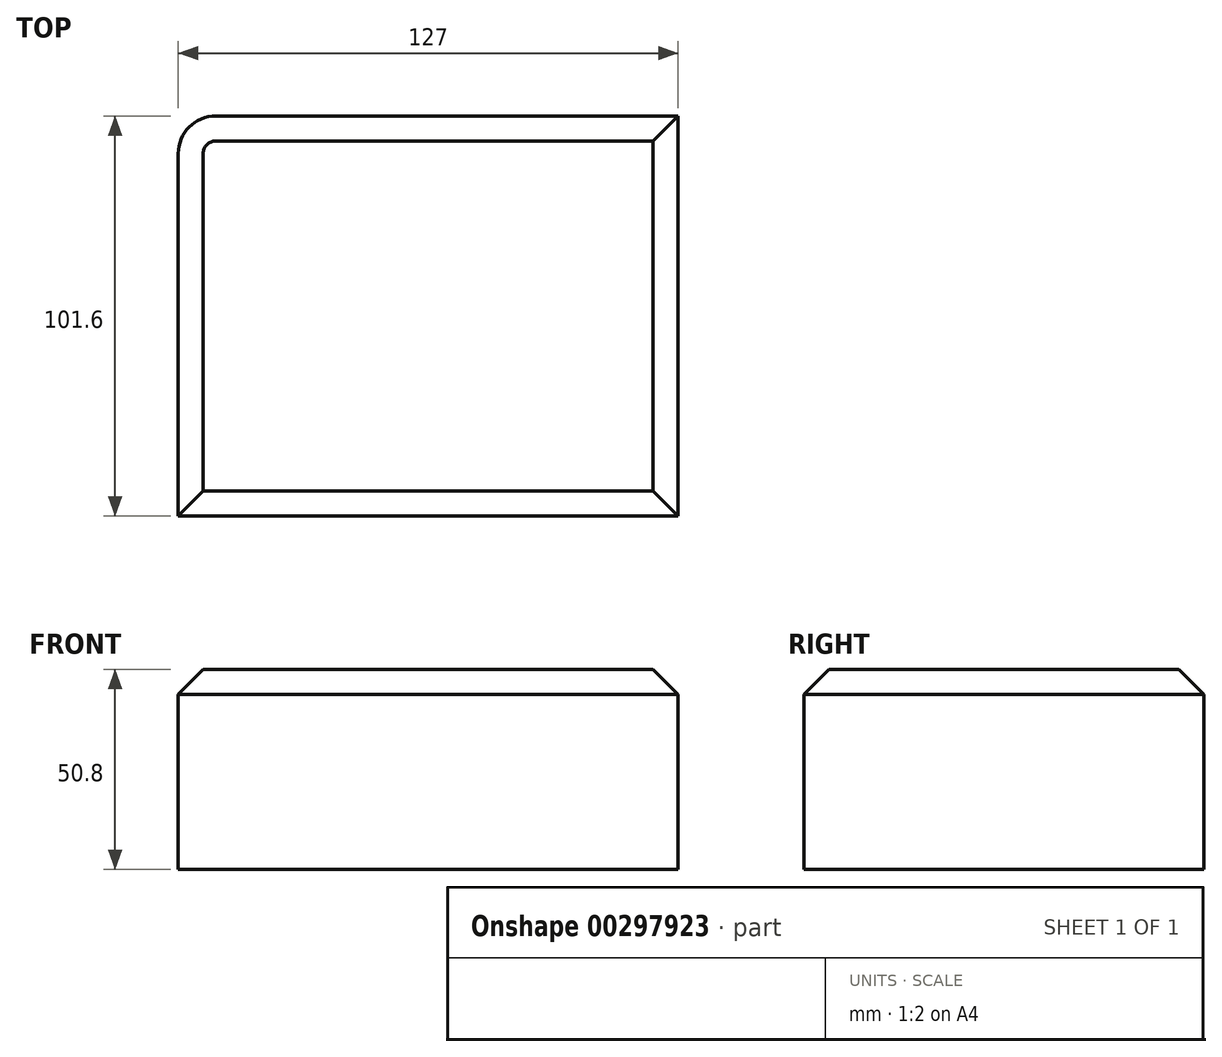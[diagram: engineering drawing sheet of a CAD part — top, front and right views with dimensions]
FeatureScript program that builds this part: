
annotation { "Feature Type Name" : "Feature", "Feature Type Description" : "" }
export const myFeature = defineFeature(function(context is Context, id is Id, definition is map)
    precondition{}
    {
        {
            var Q0;
            Q0=qCreatedBy(makeId("Top.planeOp"),FACE);
            var sketch = newSketch(context, id + "F0", { "sketchPlane" : qUnion([Q0])});
            skLineSegment(sketch, "E0.bottom", {"start": v(-53.97, 49.1) * mm, "end": v(63.5, 49.1) * mm});
            skLineSegment(sketch, "E0.top", {"start": v(-63.5, -52.5) * mm, "end": v(63.5, -52.5) * mm});
            skLineSegment(sketch, "E0.left", {"start": v(-63.5, 39.57) * mm, "end": v(-63.5, -52.5) * mm});
            skLineSegment(sketch, "E0.right", {"start": v(63.5, 49.1) * mm, "end": v(63.5, -52.5) * mm});
            skPoint(sketch, "E0.middle", {"position": v(0, -1.7) * mm});
            skPoint(sketch, "E1.visualSharp", {"position": v(-63.5, 49.1) * mm});
            skArc(sketch, "E1.filletArc", {"start": v(-53.97, 49.1) * mm, "mid": v(-60.71, 46.3) * mm, "end": v(-63.5, 39.57) * mm});
            skSolve(sketch);
        }
        {
            var Q0;
            Q0=makeQuery(id+"F0.imprint","IMPRINT",FACE,{"disambiguationData":[TD([[makeQuery(id+"F0.imprint","IMPRINT",EDGE,{"derivedFrom":sQuery(id+"F0.wireOp",EDGE,"E0.bottom")}),-1.0]])]});
            extrude(context, id + "F1", {"entities" : qUnion([Q0]), "depth" : 50.8 * mm});
        }
        {
            var Q0;
            Q0=makeQuery(id+"F1.opExtrude","CAP_EDGE",EDGE,{"disambiguationData":[OSD([sQuery(id+"F0.wireOp",EDGE,"E0.top")])],"isStart":false});
            var Q1;
            Q1=makeQuery(id+"F1.opExtrude","CAP_EDGE",EDGE,{"disambiguationData":[OSD([sQuery(id+"F0.wireOp",EDGE,"E0.right")])],"isStart":false});
            var Q2;
            Q2=makeQuery(id+"F1.opExtrude","CAP_EDGE",EDGE,{"disambiguationData":[OSD([sQuery(id+"F0.wireOp",EDGE,"E0.bottom")])],"isStart":false});
            var Q3;
            Q3=makeQuery(id+"F1.opExtrude","CAP_EDGE",EDGE,{"disambiguationData":[OSD([sQuery(id+"F0.wireOp",EDGE,"E1.filletArc")])],"isStart":false});
            var Q4;
            Q4=makeQuery(id+"F1.opExtrude","CAP_EDGE",EDGE,{"disambiguationData":[OSD([sQuery(id+"F0.wireOp",EDGE,"E0.left")])],"isStart":false});
            chamfer(context, id + "F2", {"entities" : qUnion([Q0, Q1, Q2, Q3, Q4]), "width" : 6.35 * mm, "tangentPropagation" : true});
        }
    });
